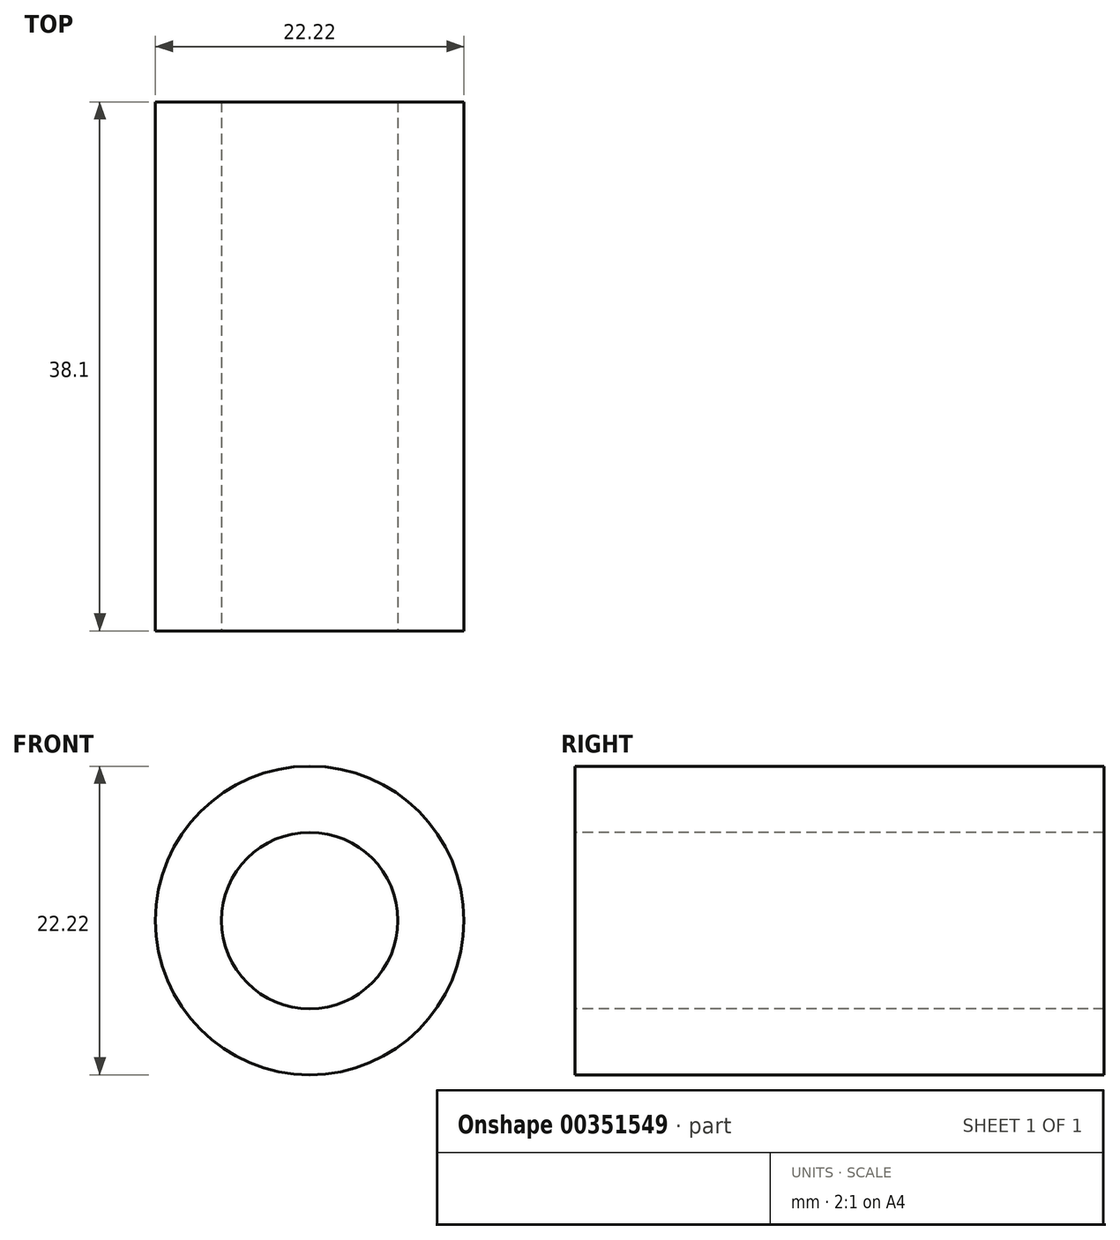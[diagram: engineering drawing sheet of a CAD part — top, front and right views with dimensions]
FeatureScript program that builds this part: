
annotation { "Feature Type Name" : "Feature", "Feature Type Description" : "" }
export const myFeature = defineFeature(function(context is Context, id is Id, definition is map)
    precondition{}
    {
        {
            var Q0;
            Q0=qCreatedBy(makeId("Front.planeOp"),FACE);
            var sketch = newSketch(context, id + "F0", { "sketchPlane" : qUnion([Q0])});
            skCircle(sketch, "E0", {"center": v(0, 0) * mm, "radius": 11.11 * mm});
            skSolve(sketch);
        }
        {
            var Q0;
            Q0 = qSketchRegion(id + "F0", true);
            extrude(context, id + "F1", {"entities" : qUnion([Q0]), "depth" : 38.1 * mm, "symmetric" : true});
        }
        {
            var Q0;
            Q0=makeQuery(id+"F1.opExtrude","CAP_FACE",FACE,{"disambiguationData":[OSD([sQuery(id+"F0.wireOp",EDGE,"E0")])],"isStart":false});
            var sketch = newSketch(context, id + "F2", { "sketchPlane" : qUnion([Q0])});
            skCircle(sketch, "E1", {"center": v(0, 0) * mm, "radius": 6.35 * mm});
            skSolve(sketch);
        }
        {
            var Q0;
            Q0 = qSketchRegion(id + "F2", true);
            extrude(context, id + "F3", {"entities" : qUnion([Q0]), "operationType" : NewBodyOperationType.REMOVE, "oppositeDirection" : true, "depth" : 38.1 * mm});
        }
    });
